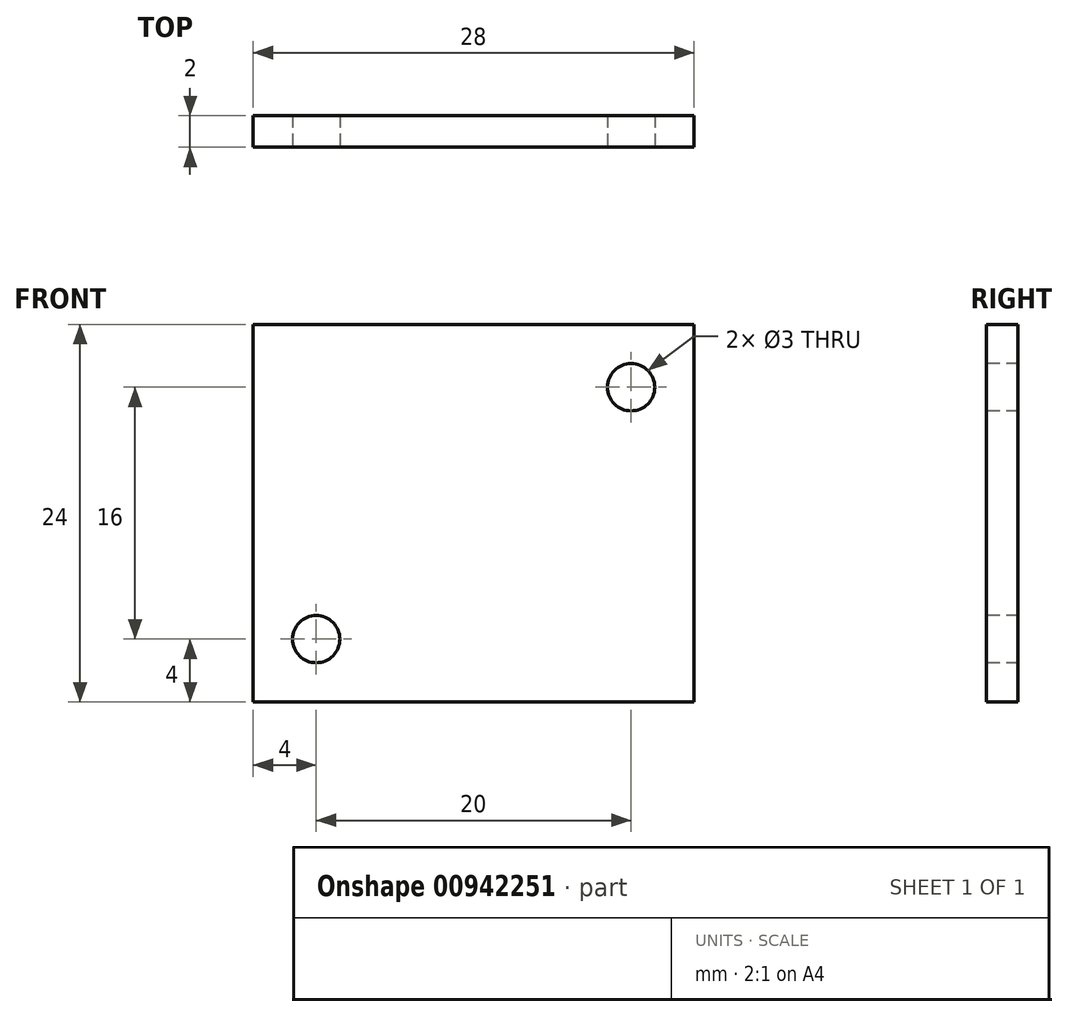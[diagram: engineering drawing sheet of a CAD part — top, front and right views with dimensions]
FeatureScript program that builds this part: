
annotation { "Feature Type Name" : "Feature", "Feature Type Description" : "" }
export const myFeature = defineFeature(function(context is Context, id is Id, definition is map)
    precondition{}
    {
        {
            var Q0;
            Q0=qCreatedBy(makeId("Front.planeOp"),FACE);
            var sketch = newSketch(context, id + "F0", { "sketchPlane" : qUnion([Q0])});
            skLineSegment(sketch, "E0.bottom", {"start": v(14, -12) * mm, "end": v(-14, -12) * mm});
            skLineSegment(sketch, "E0.top", {"start": v(14, 12) * mm, "end": v(-14, 12) * mm});
            skLineSegment(sketch, "E0.left", {"start": v(14, -12) * mm, "end": v(14, 12) * mm});
            skLineSegment(sketch, "E0.right", {"start": v(-14, -12) * mm, "end": v(-14, 12) * mm});
            skPoint(sketch, "E0.middle", {"position": v(0, 0) * mm});
            skSolve(sketch);
        }
        {
            var Q0;
            Q0 = qSketchRegion(id + "F0", true);
            extrude(context, id + "F1", {"entities" : qUnion([Q0]), "depth" : 2 * mm, "offsetDistance" : 25 * mm});
        }
        {
            var Q0;
            Q0=makeQuery(id+"F1.opExtrude","CAP_FACE",FACE,{"disambiguationData":[OSD([sQuery(id+"F0.wireOp",EDGE,"E0.bottom"),sQuery(id+"F0.wireOp",EDGE,"E0.top"),sQuery(id+"F0.wireOp",EDGE,"E0.left"),sQuery(id+"F0.wireOp",EDGE,"E0.right")])],"isStart":false});
            var sketch = newSketch(context, id + "F2", { "sketchPlane" : qUnion([Q0])});
            skPoint(sketch, "E1", {"position": v(10, 8) * mm});
            skPoint(sketch, "E2", {"position": v(-10, -8) * mm});
            skLineSegment(sketch, "E3", {"start": v(0, 0) * mm, "end": v(0, 18) * mm, "construction": true});
            skSolve(sketch);
        }
        {
            var Q0;
            Q0=sQuery(id+"F2.wireOp",VERTEX,"E2");
            var Q1;
            Q1=sQuery(id+"F2.wireOp",VERTEX,"E1");
            var Q2;
            Q2=makeQuery(id+"F1.opExtrude","SWEPT_BODY",BODY,{"disambiguationData":[OSD([sQuery(id+"F0.wireOp",EDGE,"E0.bottom"),sQuery(id+"F0.wireOp",EDGE,"E0.top"),sQuery(id+"F0.wireOp",EDGE,"E0.left"),sQuery(id+"F0.wireOp",EDGE,"E0.right")])]});
            hole(context, id + "F3", {"style" : HoleStyle.SIMPLE, "endStyle" : HoleEndStyle.THROUGH, "holeDiameter" : 3 * mm, "majorDiameter" : 5 * mm, "isTappedThrough" : true, "tappedDepth" : 8.5 * mm, "tapClearance" : 3, "startFromSketch" : true, "locations" : qUnion([Q0, Q1]), "scope" : qUnion([Q2])});
        }
    });
